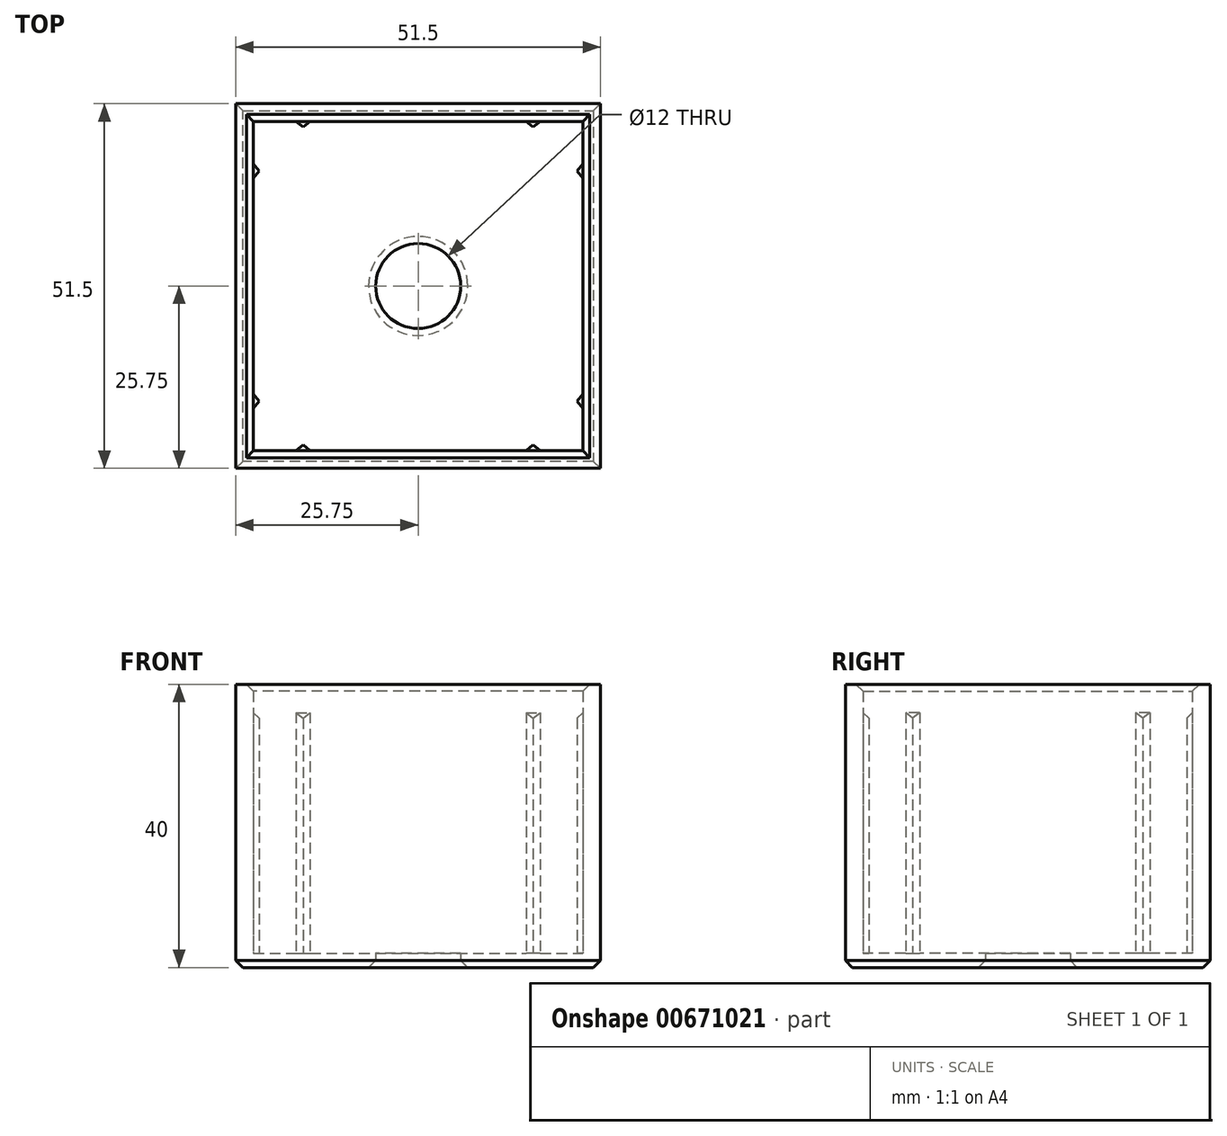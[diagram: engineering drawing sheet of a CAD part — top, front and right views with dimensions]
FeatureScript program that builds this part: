
annotation { "Feature Type Name" : "Feature", "Feature Type Description" : "" }
export const myFeature = defineFeature(function(context is Context, id is Id, definition is map)
    precondition{}
    {
        {
            var Q0;
            Q0=qCreatedBy(makeId("Top.planeOp"),FACE);
            var sketch = newSketch(context, id + "F0", { "sketchPlane" : qUnion([Q0])});
            skCircle(sketch, "E0", {"center": v(0, 0) * mm, "radius": 6 * mm});
            skLineSegment(sketch, "E1", {"start": v(-23.25, 23.25) * mm, "end": v(23.25, 23.25) * mm});
            skLineSegment(sketch, "E2", {"start": v(-25.75, 25.75) * mm, "end": v(25.75, 25.75) * mm});
            skLineSegment(sketch, "E3", {"start": v(17.25, 23.25) * mm, "end": v(16.25, 22.45) * mm});
            skLineSegment(sketch, "E4", {"start": v(16.25, 22.45) * mm, "end": v(15.25, 23.25) * mm});
            skLineSegment(sketch, "E5.MirrorCS", {"start": v(-16.25, 22.45) * mm, "end": v(-15.25, 23.25) * mm});
            skLineSegment(sketch, "E6.MirrorCS", {"start": v(-17.25, 23.25) * mm, "end": v(-16.25, 22.45) * mm});
            skLineSegment(sketch, "E7.1.0", {"start": v(-25.75, -25.75) * mm, "end": v(-25.75, 25.75) * mm});
            skLineSegment(sketch, "E7.1.1", {"start": v(-23.25, -23.25) * mm, "end": v(-23.25, 23.25) * mm});
            skLineSegment(sketch, "E7.1.2", {"start": v(-23.25, 17.25) * mm, "end": v(-22.45, 16.25) * mm});
            skLineSegment(sketch, "E7.1.3", {"start": v(-22.45, 16.25) * mm, "end": v(-23.25, 15.25) * mm});
            skLineSegment(sketch, "E7.1.4", {"start": v(-23.25, -17.25) * mm, "end": v(-22.45, -16.25) * mm});
            skLineSegment(sketch, "E7.1.5", {"start": v(-22.45, -16.25) * mm, "end": v(-23.25, -15.25) * mm});
            skLineSegment(sketch, "E7.2.0", {"start": v(25.75, -25.75) * mm, "end": v(-25.75, -25.75) * mm});
            skLineSegment(sketch, "E7.2.1", {"start": v(23.25, -23.25) * mm, "end": v(-23.25, -23.25) * mm});
            skLineSegment(sketch, "E7.2.2", {"start": v(-17.25, -23.25) * mm, "end": v(-16.25, -22.45) * mm});
            skLineSegment(sketch, "E7.2.3", {"start": v(-16.25, -22.45) * mm, "end": v(-15.25, -23.25) * mm});
            skLineSegment(sketch, "E7.2.4", {"start": v(17.25, -23.25) * mm, "end": v(16.25, -22.45) * mm});
            skLineSegment(sketch, "E7.2.5", {"start": v(16.25, -22.45) * mm, "end": v(15.25, -23.25) * mm});
            skLineSegment(sketch, "E7.3.0", {"start": v(25.75, 25.75) * mm, "end": v(25.75, -25.75) * mm});
            skLineSegment(sketch, "E7.3.1", {"start": v(23.25, 23.25) * mm, "end": v(23.25, -23.25) * mm});
            skLineSegment(sketch, "E7.3.2", {"start": v(23.25, -17.25) * mm, "end": v(22.45, -16.25) * mm});
            skLineSegment(sketch, "E7.3.3", {"start": v(22.45, -16.25) * mm, "end": v(23.25, -15.25) * mm});
            skLineSegment(sketch, "E7.3.4", {"start": v(23.25, 17.25) * mm, "end": v(22.45, 16.25) * mm});
            skLineSegment(sketch, "E7.3.5", {"start": v(22.45, 16.25) * mm, "end": v(23.25, 15.25) * mm});
            skSolve(sketch);
        }
        {
            var Q0;
            Q0 = qSketchRegion(id + "F0", true);
            extrude(context, id + "F1", {"entities" : qUnion([Q0]), "depth" : 40 * mm, "offsetDistance" : 25 * mm});
        }
        {
            var Q0;
            Q0=makeQuery(id+"F0.imprint","IMPRINT",FACE,{"disambiguationData":[TD([[makeQuery(id+"F0.imprint","IMPRINT",EDGE,{"derivedFrom":sQuery(id+"F0.wireOp",EDGE,"E2")}),-1.0]])]});
            var Q1;
            {var subQ0=sQuery(id+"F0.wireOp",EDGE,"E7.1.2");Q1=makeQuery(id+"F0.imprint","IMPRINT",FACE,{"disambiguationData":[TD([[makeQuery(id+"F0.imprint","IMPRINT",EDGE,{"derivedFrom":subQ0}),-1.0]])]});}
            var Q2;
            {var subQ0=sQuery(id+"F0.wireOp",EDGE,"E5.MirrorCS");Q2=makeQuery(id+"F0.imprint","IMPRINT",FACE,{"disambiguationData":[TD([[makeQuery(id+"F0.imprint","IMPRINT",EDGE,{"derivedFrom":subQ0}),1.0]])]});}
            var Q3;
            {var subQ0=sQuery(id+"F0.wireOp",EDGE,"E3");Q3=makeQuery(id+"F0.imprint","IMPRINT",FACE,{"disambiguationData":[TD([[makeQuery(id+"F0.imprint","IMPRINT",EDGE,{"derivedFrom":subQ0}),-1.0]])]});}
            var Q4;
            {var subQ0=sQuery(id+"F0.wireOp",EDGE,"E7.3.4");Q4=makeQuery(id+"F0.imprint","IMPRINT",FACE,{"disambiguationData":[TD([[makeQuery(id+"F0.imprint","IMPRINT",EDGE,{"derivedFrom":subQ0}),1.0]])]});}
            var Q5;
            {var subQ0=sQuery(id+"F0.wireOp",EDGE,"E7.3.2");Q5=makeQuery(id+"F0.imprint","IMPRINT",FACE,{"disambiguationData":[TD([[makeQuery(id+"F0.imprint","IMPRINT",EDGE,{"derivedFrom":subQ0}),-1.0]])]});}
            var Q6;
            {var subQ0=sQuery(id+"F0.wireOp",EDGE,"E7.2.4");Q6=makeQuery(id+"F0.imprint","IMPRINT",FACE,{"disambiguationData":[TD([[makeQuery(id+"F0.imprint","IMPRINT",EDGE,{"derivedFrom":subQ0}),1.0]])]});}
            var Q7;
            {var subQ0=sQuery(id+"F0.wireOp",EDGE,"E7.2.2");Q7=makeQuery(id+"F0.imprint","IMPRINT",FACE,{"disambiguationData":[TD([[makeQuery(id+"F0.imprint","IMPRINT",EDGE,{"derivedFrom":subQ0}),-1.0]])]});}
            var Q8;
            {var subQ0=sQuery(id+"F0.wireOp",EDGE,"E7.1.4");Q8=makeQuery(id+"F0.imprint","IMPRINT",FACE,{"disambiguationData":[TD([[makeQuery(id+"F0.imprint","IMPRINT",EDGE,{"derivedFrom":subQ0}),1.0]])]});}
            extrude(context, id + "F2", {"entities" : qUnion([Q0, Q1, Q2, Q3, Q4, Q5, Q6, Q7, Q8]), "operationType" : NewBodyOperationType.ADD, "depth" : 35 * mm, "offsetDistance" : 25 * mm});
        }
        {
            var Q0;
            Q0=makeQuery(id+"F0.imprint","IMPRINT",FACE,{"disambiguationData":[TD([[makeQuery(id+"F0.imprint","IMPRINT",EDGE,{"derivedFrom":sQuery(id+"F0.wireOp",EDGE,"E0")}),-1.0]])]});
            extrude(context, id + "F3", {"entities" : qUnion([Q0]), "operationType" : NewBodyOperationType.ADD, "depth" : 2 * mm, "offsetDistance" : 25 * mm});
        }
        {
            var Q0;
            Q0=makeQuery(id+"F1.opExtrude","CAP_EDGE",EDGE,{"disambiguationData":[OSD([sQuery(id+"F0.wireOp",EDGE,"E1")])],"isStart":false});
            var Q1;
            Q1=makeQuery(id+"F1.opExtrude","CAP_EDGE",EDGE,{"disambiguationData":[OSD([sQuery(id+"F0.wireOp",EDGE,"E7.1.1")])],"isStart":false});
            var Q2;
            Q2=makeQuery(id+"F1.opExtrude","CAP_EDGE",EDGE,{"disambiguationData":[OSD([sQuery(id+"F0.wireOp",EDGE,"E7.2.1")])],"isStart":false});
            var Q3;
            Q3=makeQuery(id+"F1.opExtrude","CAP_EDGE",EDGE,{"disambiguationData":[OSD([sQuery(id+"F0.wireOp",EDGE,"E7.3.1")])],"isStart":false});
            var Q4;
            {var subQ0=sQuery(id+"F0.wireOp",EDGE,"E7.3.5");var subQ1=sQuery(id+"F0.wireOp",EDGE,"E7.3.4");var subQ2=sQuery(id+"F0.wireOp",EDGE,"E7.3.3");var subQ3=sQuery(id+"F0.wireOp",EDGE,"E7.3.2");var subQ4=sQuery(id+"F0.wireOp",EDGE,"E7.3.1");var subQ5=sQuery(id+"F0.wireOp",EDGE,"E7.2.5");var subQ6=sQuery(id+"F0.wireOp",EDGE,"E7.2.4");var subQ7=sQuery(id+"F0.wireOp",EDGE,"E7.2.3");var subQ8=sQuery(id+"F0.wireOp",EDGE,"E7.2.2");var subQ9=sQuery(id+"F0.wireOp",EDGE,"E7.2.1");var subQ10=sQuery(id+"F0.wireOp",EDGE,"E7.1.5");var subQ11=sQuery(id+"F0.wireOp",EDGE,"E7.1.4");var subQ12=sQuery(id+"F0.wireOp",EDGE,"E7.1.3");var subQ13=sQuery(id+"F0.wireOp",EDGE,"E7.1.2");var subQ14=sQuery(id+"F0.wireOp",EDGE,"E7.1.1");var subQ15=sQuery(id+"F0.wireOp",EDGE,"E6.MirrorCS");var subQ16=sQuery(id+"F0.wireOp",EDGE,"E5.MirrorCS");var subQ17=sQuery(id+"F0.wireOp",EDGE,"E4");var subQ18=sQuery(id+"F0.wireOp",EDGE,"E3");var subQ19=sQuery(id+"F0.wireOp",EDGE,"E1");var subQ20=sQuery(id+"F0.wireOp",EDGE,"E7.3.0");var subQ21=sQuery(id+"F0.wireOp",EDGE,"E7.2.0");var subQ22=sQuery(id+"F0.wireOp",EDGE,"E7.1.0");var subQ23=sQuery(id+"F0.wireOp",EDGE,"E2");Q4=makeQuery(id+"F3.boolean.opBoolean","MERGE",FACE,{"derivedFrom":[makeQuery(id+"F2.boolean.opBoolean","MERGE",FACE,{"derivedFrom":[makeQuery(id+"F1.opExtrude","CAP_FACE",FACE,{"disambiguationData":[OSD([subQ19,subQ23,subQ22,subQ14,subQ21,subQ9,subQ20,subQ4])],"isStart":true}),makeQuery(id+"F2.opExtrude","CAP_FACE",FACE,{"disambiguationData":[OSD([subQ19,subQ23,subQ18,subQ17,subQ16,subQ15,subQ22,subQ14,subQ13,subQ12,subQ11,subQ10,subQ21,subQ9,subQ8,subQ7,subQ6,subQ5,subQ20,subQ4,subQ3,subQ2,subQ1,subQ0])],"isStart":true})]}),makeQuery(id+"F3.opExtrude","CAP_FACE",FACE,{"disambiguationData":[OSD([sQuery(id+"F0.wireOp",EDGE,"E0"),subQ19,subQ18,subQ17,subQ16,subQ15,subQ14,subQ13,subQ12,subQ11,subQ10,subQ9,subQ8,subQ7,subQ6,subQ5,subQ4,subQ3,subQ2,subQ1,subQ0])],"isStart":true})]});}
            var Q5;
            {var subQ0=sQuery(id+"F0.wireOp",EDGE,"E1");Q5=makeQuery(id+"F2.boolean.opBoolean","INTERSECT",EDGE,{"disambiguationData":[OD(0.0)],"derivedFrom":[makeQuery(id+"F1.opExtrude","SWEPT_FACE",FACE,{"disambiguationData":[OSD([subQ0])]}),makeQuery(id+"F2.opExtrude","CAP_FACE",FACE,{"disambiguationData":[OSD([subQ0,sQuery(id+"F0.wireOp",EDGE,"E2"),sQuery(id+"F0.wireOp",EDGE,"E3"),sQuery(id+"F0.wireOp",EDGE,"E4"),sQuery(id+"F0.wireOp",EDGE,"E5.MirrorCS"),sQuery(id+"F0.wireOp",EDGE,"E6.MirrorCS"),sQuery(id+"F0.wireOp",EDGE,"E7.1.0"),sQuery(id+"F0.wireOp",EDGE,"E7.1.1"),sQuery(id+"F0.wireOp",EDGE,"E7.1.2"),sQuery(id+"F0.wireOp",EDGE,"E7.1.3"),sQuery(id+"F0.wireOp",EDGE,"E7.1.4"),sQuery(id+"F0.wireOp",EDGE,"E7.1.5"),sQuery(id+"F0.wireOp",EDGE,"E7.2.0"),sQuery(id+"F0.wireOp",EDGE,"E7.2.1"),sQuery(id+"F0.wireOp",EDGE,"E7.2.2"),sQuery(id+"F0.wireOp",EDGE,"E7.2.3"),sQuery(id+"F0.wireOp",EDGE,"E7.2.4"),sQuery(id+"F0.wireOp",EDGE,"E7.2.5"),sQuery(id+"F0.wireOp",EDGE,"E7.3.0"),sQuery(id+"F0.wireOp",EDGE,"E7.3.1"),sQuery(id+"F0.wireOp",EDGE,"E7.3.2"),sQuery(id+"F0.wireOp",EDGE,"E7.3.3"),sQuery(id+"F0.wireOp",EDGE,"E7.3.4"),sQuery(id+"F0.wireOp",EDGE,"E7.3.5")])],"isStart":false})]});}
            var Q6;
            {var subQ0=sQuery(id+"F0.wireOp",EDGE,"E1");Q6=makeQuery(id+"F2.boolean.opBoolean","INTERSECT",EDGE,{"disambiguationData":[OD(1.0)],"derivedFrom":[makeQuery(id+"F1.opExtrude","SWEPT_FACE",FACE,{"disambiguationData":[OSD([subQ0])]}),makeQuery(id+"F2.opExtrude","CAP_FACE",FACE,{"disambiguationData":[OSD([subQ0,sQuery(id+"F0.wireOp",EDGE,"E2"),sQuery(id+"F0.wireOp",EDGE,"E3"),sQuery(id+"F0.wireOp",EDGE,"E4"),sQuery(id+"F0.wireOp",EDGE,"E5.MirrorCS"),sQuery(id+"F0.wireOp",EDGE,"E6.MirrorCS"),sQuery(id+"F0.wireOp",EDGE,"E7.1.0"),sQuery(id+"F0.wireOp",EDGE,"E7.1.1"),sQuery(id+"F0.wireOp",EDGE,"E7.1.2"),sQuery(id+"F0.wireOp",EDGE,"E7.1.3"),sQuery(id+"F0.wireOp",EDGE,"E7.1.4"),sQuery(id+"F0.wireOp",EDGE,"E7.1.5"),sQuery(id+"F0.wireOp",EDGE,"E7.2.0"),sQuery(id+"F0.wireOp",EDGE,"E7.2.1"),sQuery(id+"F0.wireOp",EDGE,"E7.2.2"),sQuery(id+"F0.wireOp",EDGE,"E7.2.3"),sQuery(id+"F0.wireOp",EDGE,"E7.2.4"),sQuery(id+"F0.wireOp",EDGE,"E7.2.5"),sQuery(id+"F0.wireOp",EDGE,"E7.3.0"),sQuery(id+"F0.wireOp",EDGE,"E7.3.1"),sQuery(id+"F0.wireOp",EDGE,"E7.3.2"),sQuery(id+"F0.wireOp",EDGE,"E7.3.3"),sQuery(id+"F0.wireOp",EDGE,"E7.3.4"),sQuery(id+"F0.wireOp",EDGE,"E7.3.5")])],"isStart":false})]});}
            var Q7;
            {var subQ0=sQuery(id+"F0.wireOp",EDGE,"E7.3.1");Q7=makeQuery(id+"F2.boolean.opBoolean","INTERSECT",EDGE,{"disambiguationData":[OD(1.0)],"derivedFrom":[makeQuery(id+"F1.opExtrude","SWEPT_FACE",FACE,{"disambiguationData":[OSD([subQ0])]}),makeQuery(id+"F2.opExtrude","CAP_FACE",FACE,{"disambiguationData":[OSD([sQuery(id+"F0.wireOp",EDGE,"E1"),sQuery(id+"F0.wireOp",EDGE,"E2"),sQuery(id+"F0.wireOp",EDGE,"E3"),sQuery(id+"F0.wireOp",EDGE,"E4"),sQuery(id+"F0.wireOp",EDGE,"E5.MirrorCS"),sQuery(id+"F0.wireOp",EDGE,"E6.MirrorCS"),sQuery(id+"F0.wireOp",EDGE,"E7.1.0"),sQuery(id+"F0.wireOp",EDGE,"E7.1.1"),sQuery(id+"F0.wireOp",EDGE,"E7.1.2"),sQuery(id+"F0.wireOp",EDGE,"E7.1.3"),sQuery(id+"F0.wireOp",EDGE,"E7.1.4"),sQuery(id+"F0.wireOp",EDGE,"E7.1.5"),sQuery(id+"F0.wireOp",EDGE,"E7.2.0"),sQuery(id+"F0.wireOp",EDGE,"E7.2.1"),sQuery(id+"F0.wireOp",EDGE,"E7.2.2"),sQuery(id+"F0.wireOp",EDGE,"E7.2.3"),sQuery(id+"F0.wireOp",EDGE,"E7.2.4"),sQuery(id+"F0.wireOp",EDGE,"E7.2.5"),sQuery(id+"F0.wireOp",EDGE,"E7.3.0"),subQ0,sQuery(id+"F0.wireOp",EDGE,"E7.3.2"),sQuery(id+"F0.wireOp",EDGE,"E7.3.3"),sQuery(id+"F0.wireOp",EDGE,"E7.3.4"),sQuery(id+"F0.wireOp",EDGE,"E7.3.5")])],"isStart":false})]});}
            var Q8;
            {var subQ0=sQuery(id+"F0.wireOp",EDGE,"E7.3.1");Q8=makeQuery(id+"F2.boolean.opBoolean","INTERSECT",EDGE,{"disambiguationData":[OD(0.0)],"derivedFrom":[makeQuery(id+"F1.opExtrude","SWEPT_FACE",FACE,{"disambiguationData":[OSD([subQ0])]}),makeQuery(id+"F2.opExtrude","CAP_FACE",FACE,{"disambiguationData":[OSD([sQuery(id+"F0.wireOp",EDGE,"E1"),sQuery(id+"F0.wireOp",EDGE,"E2"),sQuery(id+"F0.wireOp",EDGE,"E3"),sQuery(id+"F0.wireOp",EDGE,"E4"),sQuery(id+"F0.wireOp",EDGE,"E5.MirrorCS"),sQuery(id+"F0.wireOp",EDGE,"E6.MirrorCS"),sQuery(id+"F0.wireOp",EDGE,"E7.1.0"),sQuery(id+"F0.wireOp",EDGE,"E7.1.1"),sQuery(id+"F0.wireOp",EDGE,"E7.1.2"),sQuery(id+"F0.wireOp",EDGE,"E7.1.3"),sQuery(id+"F0.wireOp",EDGE,"E7.1.4"),sQuery(id+"F0.wireOp",EDGE,"E7.1.5"),sQuery(id+"F0.wireOp",EDGE,"E7.2.0"),sQuery(id+"F0.wireOp",EDGE,"E7.2.1"),sQuery(id+"F0.wireOp",EDGE,"E7.2.2"),sQuery(id+"F0.wireOp",EDGE,"E7.2.3"),sQuery(id+"F0.wireOp",EDGE,"E7.2.4"),sQuery(id+"F0.wireOp",EDGE,"E7.2.5"),sQuery(id+"F0.wireOp",EDGE,"E7.3.0"),subQ0,sQuery(id+"F0.wireOp",EDGE,"E7.3.2"),sQuery(id+"F0.wireOp",EDGE,"E7.3.3"),sQuery(id+"F0.wireOp",EDGE,"E7.3.4"),sQuery(id+"F0.wireOp",EDGE,"E7.3.5")])],"isStart":false})]});}
            var Q9;
            {var subQ0=sQuery(id+"F0.wireOp",EDGE,"E7.1.1");Q9=makeQuery(id+"F2.boolean.opBoolean","INTERSECT",EDGE,{"disambiguationData":[OD(0.0)],"derivedFrom":[makeQuery(id+"F1.opExtrude","SWEPT_FACE",FACE,{"disambiguationData":[OSD([subQ0])]}),makeQuery(id+"F2.opExtrude","CAP_FACE",FACE,{"disambiguationData":[OSD([sQuery(id+"F0.wireOp",EDGE,"E1"),sQuery(id+"F0.wireOp",EDGE,"E2"),sQuery(id+"F0.wireOp",EDGE,"E3"),sQuery(id+"F0.wireOp",EDGE,"E4"),sQuery(id+"F0.wireOp",EDGE,"E5.MirrorCS"),sQuery(id+"F0.wireOp",EDGE,"E6.MirrorCS"),sQuery(id+"F0.wireOp",EDGE,"E7.1.0"),subQ0,sQuery(id+"F0.wireOp",EDGE,"E7.1.2"),sQuery(id+"F0.wireOp",EDGE,"E7.1.3"),sQuery(id+"F0.wireOp",EDGE,"E7.1.4"),sQuery(id+"F0.wireOp",EDGE,"E7.1.5"),sQuery(id+"F0.wireOp",EDGE,"E7.2.0"),sQuery(id+"F0.wireOp",EDGE,"E7.2.1"),sQuery(id+"F0.wireOp",EDGE,"E7.2.2"),sQuery(id+"F0.wireOp",EDGE,"E7.2.3"),sQuery(id+"F0.wireOp",EDGE,"E7.2.4"),sQuery(id+"F0.wireOp",EDGE,"E7.2.5"),sQuery(id+"F0.wireOp",EDGE,"E7.3.0"),sQuery(id+"F0.wireOp",EDGE,"E7.3.1"),sQuery(id+"F0.wireOp",EDGE,"E7.3.2"),sQuery(id+"F0.wireOp",EDGE,"E7.3.3"),sQuery(id+"F0.wireOp",EDGE,"E7.3.4"),sQuery(id+"F0.wireOp",EDGE,"E7.3.5")])],"isStart":false})]});}
            var Q10;
            {var subQ0=sQuery(id+"F0.wireOp",EDGE,"E7.1.1");Q10=makeQuery(id+"F2.boolean.opBoolean","INTERSECT",EDGE,{"disambiguationData":[OD(1.0)],"derivedFrom":[makeQuery(id+"F1.opExtrude","SWEPT_FACE",FACE,{"disambiguationData":[OSD([subQ0])]}),makeQuery(id+"F2.opExtrude","CAP_FACE",FACE,{"disambiguationData":[OSD([sQuery(id+"F0.wireOp",EDGE,"E1"),sQuery(id+"F0.wireOp",EDGE,"E2"),sQuery(id+"F0.wireOp",EDGE,"E3"),sQuery(id+"F0.wireOp",EDGE,"E4"),sQuery(id+"F0.wireOp",EDGE,"E5.MirrorCS"),sQuery(id+"F0.wireOp",EDGE,"E6.MirrorCS"),sQuery(id+"F0.wireOp",EDGE,"E7.1.0"),subQ0,sQuery(id+"F0.wireOp",EDGE,"E7.1.2"),sQuery(id+"F0.wireOp",EDGE,"E7.1.3"),sQuery(id+"F0.wireOp",EDGE,"E7.1.4"),sQuery(id+"F0.wireOp",EDGE,"E7.1.5"),sQuery(id+"F0.wireOp",EDGE,"E7.2.0"),sQuery(id+"F0.wireOp",EDGE,"E7.2.1"),sQuery(id+"F0.wireOp",EDGE,"E7.2.2"),sQuery(id+"F0.wireOp",EDGE,"E7.2.3"),sQuery(id+"F0.wireOp",EDGE,"E7.2.4"),sQuery(id+"F0.wireOp",EDGE,"E7.2.5"),sQuery(id+"F0.wireOp",EDGE,"E7.3.0"),sQuery(id+"F0.wireOp",EDGE,"E7.3.1"),sQuery(id+"F0.wireOp",EDGE,"E7.3.2"),sQuery(id+"F0.wireOp",EDGE,"E7.3.3"),sQuery(id+"F0.wireOp",EDGE,"E7.3.4"),sQuery(id+"F0.wireOp",EDGE,"E7.3.5")])],"isStart":false})]});}
            var Q11;
            {var subQ0=sQuery(id+"F0.wireOp",EDGE,"E7.2.1");Q11=makeQuery(id+"F2.boolean.opBoolean","INTERSECT",EDGE,{"disambiguationData":[OD(0.0)],"derivedFrom":[makeQuery(id+"F1.opExtrude","SWEPT_FACE",FACE,{"disambiguationData":[OSD([subQ0])]}),makeQuery(id+"F2.opExtrude","CAP_FACE",FACE,{"disambiguationData":[OSD([sQuery(id+"F0.wireOp",EDGE,"E1"),sQuery(id+"F0.wireOp",EDGE,"E2"),sQuery(id+"F0.wireOp",EDGE,"E3"),sQuery(id+"F0.wireOp",EDGE,"E4"),sQuery(id+"F0.wireOp",EDGE,"E5.MirrorCS"),sQuery(id+"F0.wireOp",EDGE,"E6.MirrorCS"),sQuery(id+"F0.wireOp",EDGE,"E7.1.0"),sQuery(id+"F0.wireOp",EDGE,"E7.1.1"),sQuery(id+"F0.wireOp",EDGE,"E7.1.2"),sQuery(id+"F0.wireOp",EDGE,"E7.1.3"),sQuery(id+"F0.wireOp",EDGE,"E7.1.4"),sQuery(id+"F0.wireOp",EDGE,"E7.1.5"),sQuery(id+"F0.wireOp",EDGE,"E7.2.0"),subQ0,sQuery(id+"F0.wireOp",EDGE,"E7.2.2"),sQuery(id+"F0.wireOp",EDGE,"E7.2.3"),sQuery(id+"F0.wireOp",EDGE,"E7.2.4"),sQuery(id+"F0.wireOp",EDGE,"E7.2.5"),sQuery(id+"F0.wireOp",EDGE,"E7.3.0"),sQuery(id+"F0.wireOp",EDGE,"E7.3.1"),sQuery(id+"F0.wireOp",EDGE,"E7.3.2"),sQuery(id+"F0.wireOp",EDGE,"E7.3.3"),sQuery(id+"F0.wireOp",EDGE,"E7.3.4"),sQuery(id+"F0.wireOp",EDGE,"E7.3.5")])],"isStart":false})]});}
            var Q12;
            {var subQ0=sQuery(id+"F0.wireOp",EDGE,"E7.2.1");Q12=makeQuery(id+"F2.boolean.opBoolean","INTERSECT",EDGE,{"disambiguationData":[OD(1.0)],"derivedFrom":[makeQuery(id+"F1.opExtrude","SWEPT_FACE",FACE,{"disambiguationData":[OSD([subQ0])]}),makeQuery(id+"F2.opExtrude","CAP_FACE",FACE,{"disambiguationData":[OSD([sQuery(id+"F0.wireOp",EDGE,"E1"),sQuery(id+"F0.wireOp",EDGE,"E2"),sQuery(id+"F0.wireOp",EDGE,"E3"),sQuery(id+"F0.wireOp",EDGE,"E4"),sQuery(id+"F0.wireOp",EDGE,"E5.MirrorCS"),sQuery(id+"F0.wireOp",EDGE,"E6.MirrorCS"),sQuery(id+"F0.wireOp",EDGE,"E7.1.0"),sQuery(id+"F0.wireOp",EDGE,"E7.1.1"),sQuery(id+"F0.wireOp",EDGE,"E7.1.2"),sQuery(id+"F0.wireOp",EDGE,"E7.1.3"),sQuery(id+"F0.wireOp",EDGE,"E7.1.4"),sQuery(id+"F0.wireOp",EDGE,"E7.1.5"),sQuery(id+"F0.wireOp",EDGE,"E7.2.0"),subQ0,sQuery(id+"F0.wireOp",EDGE,"E7.2.2"),sQuery(id+"F0.wireOp",EDGE,"E7.2.3"),sQuery(id+"F0.wireOp",EDGE,"E7.2.4"),sQuery(id+"F0.wireOp",EDGE,"E7.2.5"),sQuery(id+"F0.wireOp",EDGE,"E7.3.0"),sQuery(id+"F0.wireOp",EDGE,"E7.3.1"),sQuery(id+"F0.wireOp",EDGE,"E7.3.2"),sQuery(id+"F0.wireOp",EDGE,"E7.3.3"),sQuery(id+"F0.wireOp",EDGE,"E7.3.4"),sQuery(id+"F0.wireOp",EDGE,"E7.3.5")])],"isStart":false})]});}
            chamfer(context, id + "F4", {"entities" : qUnion([Q0, Q1, Q2, Q3, Q4, Q5, Q6, Q7, Q8, Q9, Q10, Q11, Q12]), "width" : 1 * mm, "tangentPropagation" : true});
        }
    });
